FCSTD DOCUMENT  (FreeCAD 0.20R29177 (Git))
Label: pin
License: All rights reserved
LicenseURL: http://en.wikipedia.org/wiki/All_rights_reserved
objects: Sketcher::SketchObject×1
note: 1 computed .brp shape members not serialized (recipe doc carries the construction recipe); baked Part::Feature solids carry a one-line shape summary decoded from their .brp

FEATURE [Sketcher::SketchObject] Sketch
  FullyConstrained = false
  sketch-geometry (4):
    g0: ArcOfCircle CenterX=0 CenterY=0 CenterZ=0 NormalX=0 NormalY=0 NormalZ=1 AngleXU=0 Radius=18 StartAngle=5.61699 EndAngle=10.091
    g1: ArcOfCircle CenterX=0 CenterY=-36 CenterZ=0 NormalX=0 NormalY=0 NormalZ=1 AngleXU=0 Radius=0.5 StartAngle=3.47536 EndAngle=5.94942
    g2: ArcOfCircle CenterX=81.9404 CenterY=-64.4122 CenterZ=0 NormalX=0 NormalY=0 NormalZ=1 AngleXU=0 Radius=86.2265 StartAngle=2.47539 EndAngle=2.80782
    g3: ArcOfCircle CenterX=-81.9404 CenterY=-64.4122 CenterZ=0 NormalX=0 NormalY=0 NormalZ=1 AngleXU=0 Radius=86.2265 StartAngle=0.333769 EndAngle=0.666199
  constraints (9):
    c: Coincident(g0,g-1)
    c: Tangent(g2,g0) = 1.5708
    c: Tangent(g3,g0) = 1.5708
    c: Tangent(g2,g1) = 1.5708
    c: Tangent(g3,g1) = 1.5708
    c: Symmetric(g1,g1,g-2)
    c: Diameter(g1) = 1
    c: Diameter(g0) = 36
    c: DistanceY(g1,g0) = 36
